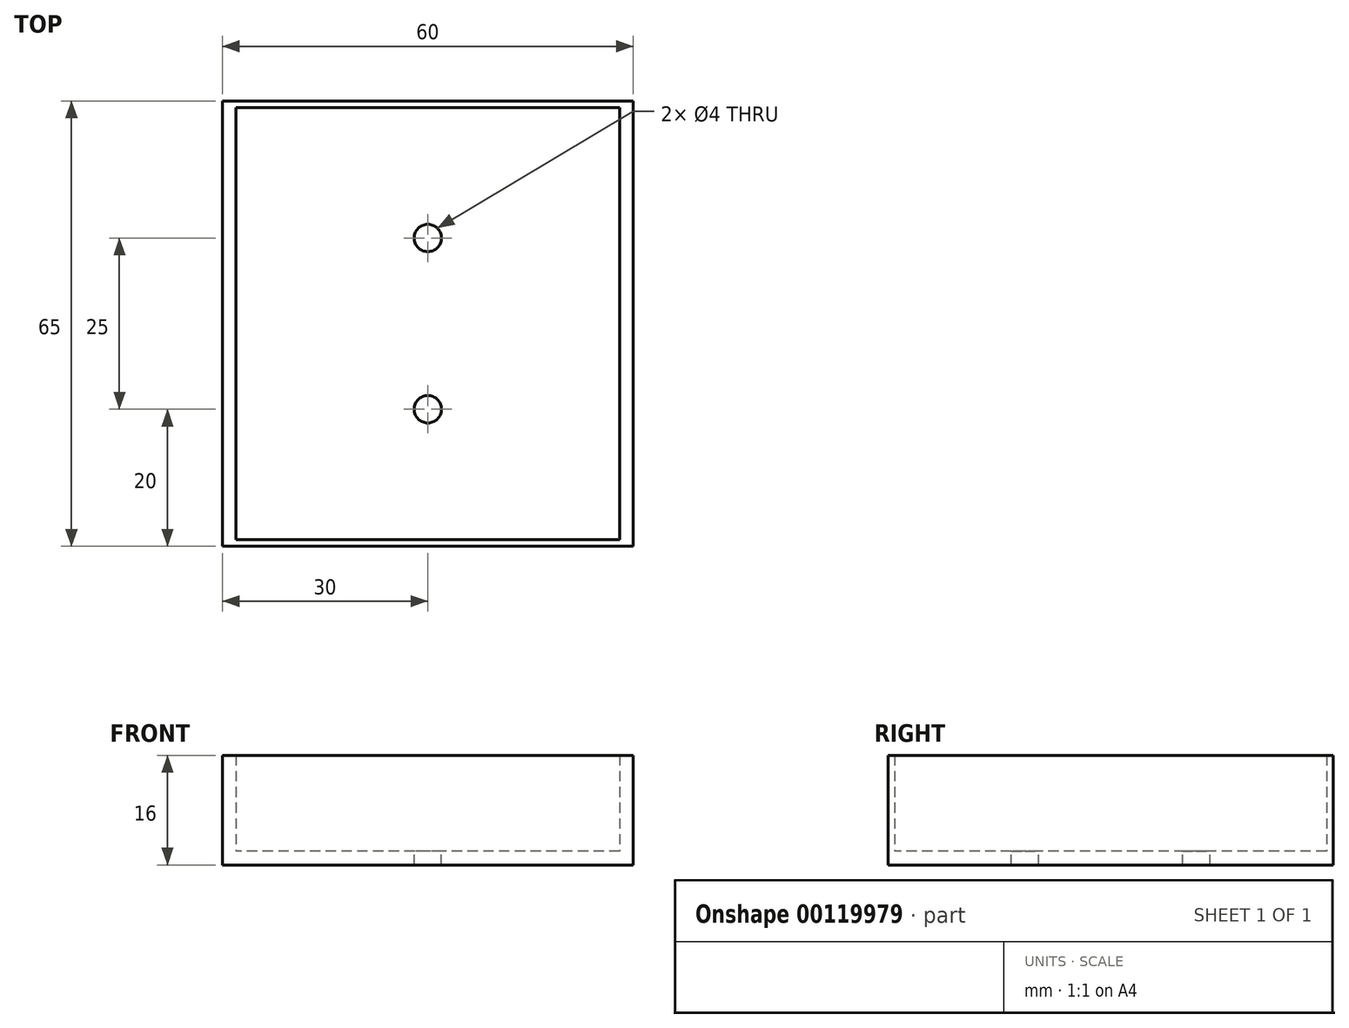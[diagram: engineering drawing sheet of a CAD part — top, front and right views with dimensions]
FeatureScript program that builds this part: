
annotation { "Feature Type Name" : "Feature", "Feature Type Description" : "" }
export const myFeature = defineFeature(function(context is Context, id is Id, definition is map)
    precondition{}
    {
        {
            var Q0;
            Q0=qCreatedBy(makeId("Top.planeOp"),FACE);
            var sketch = newSketch(context, id + "F0", { "sketchPlane" : qUnion([Q0])});
            skLineSegment(sketch, "E0.bottom", {"start": v(0, 0) * mm, "end": v(-60, 0) * mm});
            skLineSegment(sketch, "E0.top", {"start": v(0, -65) * mm, "end": v(-60, -65) * mm});
            skLineSegment(sketch, "E0.left", {"start": v(0, 0) * mm, "end": v(0, -65) * mm});
            skLineSegment(sketch, "E0.right", {"start": v(-60, 0) * mm, "end": v(-60, -65) * mm});
            skLineSegment(sketch, "E1.bottom", {"start": v(-2, -1) * mm, "end": v(-58, -1) * mm});
            skLineSegment(sketch, "E1.top", {"start": v(-2, -64) * mm, "end": v(-58, -64) * mm});
            skLineSegment(sketch, "E1.left", {"start": v(-2, -1) * mm, "end": v(-2, -64) * mm});
            skLineSegment(sketch, "E1.right", {"start": v(-58, -1) * mm, "end": v(-58, -64) * mm});
            skSolve(sketch);
        }
        {
            var Q0;
            Q0=makeQuery(id+"F0.imprint","IMPRINT",FACE,{"disambiguationData":[TD([[makeQuery(id+"F0.imprint","IMPRINT",EDGE,{"derivedFrom":sQuery(id+"F0.wireOp",EDGE,"E1.bottom")}),1.0]])]});
            extrude(context, id + "F1", {"entities" : qUnion([Q0]), "depth" : 2 * mm});
        }
        {
            var Q0;
            Q0 = qSketchRegion(id + "F0", true);
            extrude(context, id + "F2", {"entities" : qUnion([Q0]), "operationType" : NewBodyOperationType.ADD, "depth" : 16 * mm});
        }
        {
            var Q0;
            Q0=makeQuery(id+"F1.opExtrude","CAP_FACE",FACE,{"disambiguationData":[OSD([sQuery(id+"F0.wireOp",EDGE,"E1.bottom"),sQuery(id+"F0.wireOp",EDGE,"E1.top"),sQuery(id+"F0.wireOp",EDGE,"E1.left"),sQuery(id+"F0.wireOp",EDGE,"E1.right")])],"isStart":false});
            var sketch = newSketch(context, id + "F3", { "sketchPlane" : qUnion([Q0])});
            skCircle(sketch, "E2", {"center": v(-30, -20) * mm, "radius": 2 * mm});
            skPoint(sketch, "E2.centerSnap0", {"position": v(-30, -1) * mm});
            skCircle(sketch, "E3", {"center": v(-30, -45) * mm, "radius": 2 * mm});
            skSolve(sketch);
        }
        {
            var Q0;
            Q0=makeQuery(id+"F3.imprint","IMPRINT",FACE,{"disambiguationData":[TD([[makeQuery(id+"F3.imprint","IMPRINT",EDGE,{"derivedFrom":sQuery(id+"F3.wireOp",EDGE,"E2")}),1.0]])]});
            var Q1;
            Q1=makeQuery(id+"F3.imprint","IMPRINT",FACE,{"disambiguationData":[TD([[makeQuery(id+"F3.imprint","IMPRINT",EDGE,{"derivedFrom":sQuery(id+"F3.wireOp",EDGE,"E3")}),1.0]])]});
            extrude(context, id + "F4", {"entities" : qUnion([Q0, Q1]), "operationType" : NewBodyOperationType.REMOVE, "oppositeDirection" : true, "depth" : 25 * mm});
        }
    });
